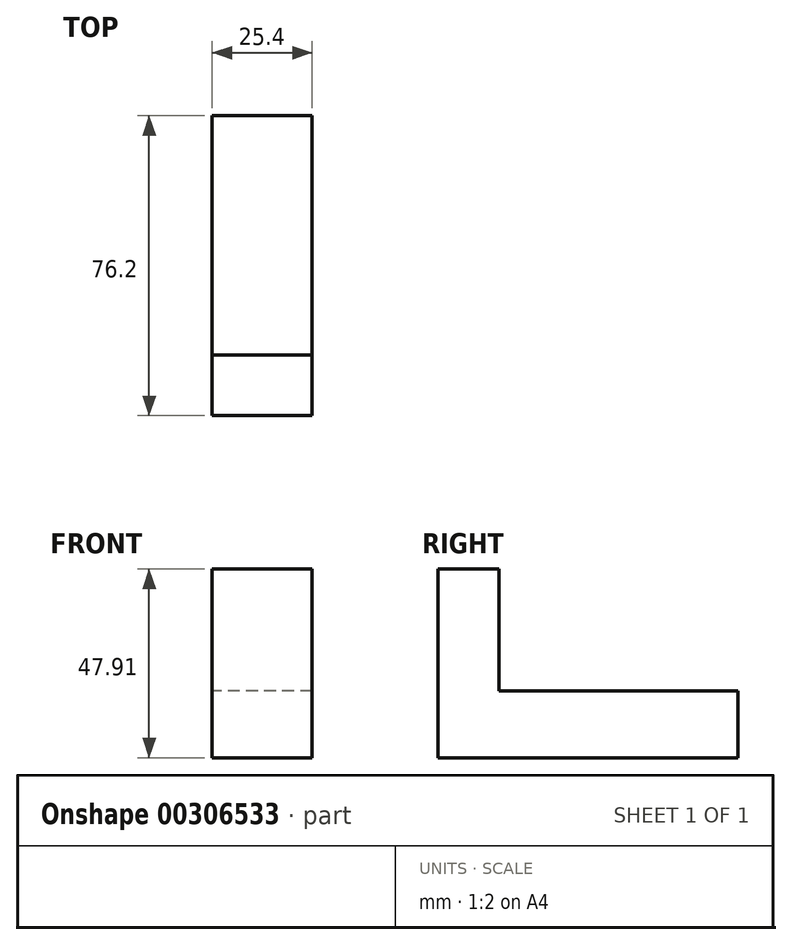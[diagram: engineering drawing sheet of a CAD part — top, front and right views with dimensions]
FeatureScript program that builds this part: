
annotation { "Feature Type Name" : "Feature", "Feature Type Description" : "" }
export const myFeature = defineFeature(function(context is Context, id is Id, definition is map)
    precondition{}
    {
        {
            var Q0;
            Q0=qCreatedBy(makeId("Right.planeOp"),FACE);
            var sketch = newSketch(context, id + "F0", { "sketchPlane" : qUnion([Q0])});
            skLineSegment(sketch, "E0", {"start": v(0, 0) * mm, "end": v(0, 47.91) * mm});
            skLineSegment(sketch, "E1", {"start": v(0, 47.91) * mm, "end": v(15.46, 47.91) * mm});
            skLineSegment(sketch, "E2", {"start": v(15.46, 47.91) * mm, "end": v(15.46, 17) * mm});
            skLineSegment(sketch, "E3", {"start": v(15.46, 17) * mm, "end": v(76.2, 17) * mm});
            skLineSegment(sketch, "E4", {"start": v(76.2, 17) * mm, "end": v(76.2, 0) * mm});
            skLineSegment(sketch, "E5", {"start": v(76.2, 0) * mm, "end": v(0, 0) * mm});
            skSolve(sketch);
        }
        {
            var Q0;
            Q0 = qSketchRegion(id + "F0", true);
            extrude(context, id + "F1", {"entities" : qUnion([Q0]), "depth" : 25.4 * mm});
        }
    });
